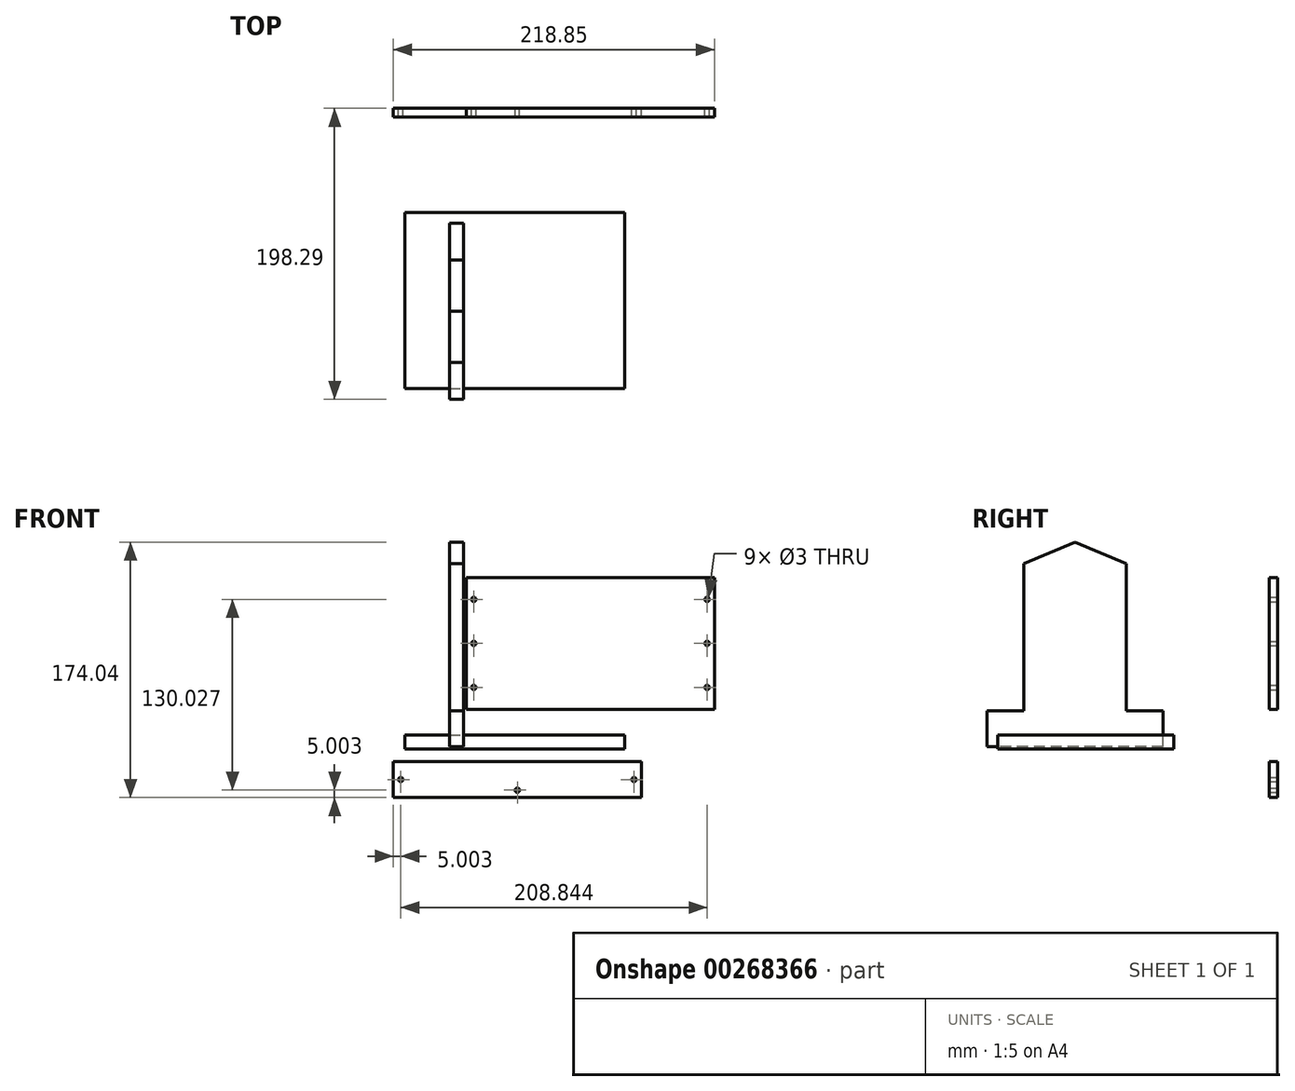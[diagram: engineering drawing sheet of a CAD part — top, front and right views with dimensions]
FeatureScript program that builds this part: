
annotation { "Feature Type Name" : "Feature", "Feature Type Description" : "" }
export const myFeature = defineFeature(function(context is Context, id is Id, definition is map)
    precondition{}
    {
        {
            var Q0;
            Q0=qCreatedBy(makeId("Top.planeOp"),FACE);
            var sketch = newSketch(context, id + "F0", { "sketchPlane" : qUnion([Q0])});
            skLineSegment(sketch, "E0.bottom", {"start": v(-30.55, -70.86) * mm, "end": v(119.45, -70.86) * mm});
            skLineSegment(sketch, "E0.top", {"start": v(-30.55, -190.86) * mm, "end": v(119.45, -190.86) * mm});
            skLineSegment(sketch, "E0.left", {"start": v(-30.55, -70.86) * mm, "end": v(-30.55, -190.86) * mm});
            skLineSegment(sketch, "E0.right", {"start": v(119.45, -70.86) * mm, "end": v(119.45, -190.86) * mm});
            skSolve(sketch);
        }
        {
            var Q0;
            Q0 = qSketchRegion(id + "F0", true);
            extrude(context, id + "F1", {"entities" : qUnion([Q0]), "depth" : 9.5 * mm});
        }
        {
            var Q0;
            Q0=qCreatedBy(makeId("Right.planeOp"),FACE);
            var sketch = newSketch(context, id + "F2", { "sketchPlane" : qUnion([Q0])});
            skLineSegment(sketch, "E1.bottom", {"start": v(-103.3, 1.37) * mm, "end": v(-173.3, 1.37) * mm});
            skLineSegment(sketch, "E1.left", {"start": v(-103.3, 25.87) * mm, "end": v(-103.3, 126.38) * mm});
            skLineSegment(sketch, "E1.right", {"start": v(-173.3, 25.87) * mm, "end": v(-173.3, 126.38) * mm});
            skLineSegment(sketch, "E2", {"start": v(-138.3, 140.87) * mm, "end": v(-103.3, 126.38) * mm});
            skLineSegment(sketch, "E3", {"start": v(-138.3, 140.87) * mm, "end": v(-173.3, 126.38) * mm});
            skPoint(sketch, "E4.orphan", {"position": v(-173.3, 140.87) * mm});
            skPoint(sketch, "E5.orphan", {"position": v(-103.3, 140.87) * mm});
            skLineSegment(sketch, "E6", {"start": v(-173.3, 1.37) * mm, "end": v(-198.3, 1.37) * mm});
            skLineSegment(sketch, "E7", {"start": v(-198.3, 1.37) * mm, "end": v(-198.3, 25.87) * mm});
            skLineSegment(sketch, "E8", {"start": v(-198.3, 25.87) * mm, "end": v(-173.3, 25.87) * mm});
            skLineSegment(sketch, "E9", {"start": v(-103.3, 1.37) * mm, "end": v(-78.3, 1.37) * mm});
            skLineSegment(sketch, "E10", {"start": v(-78.3, 1.37) * mm, "end": v(-78.3, 25.87) * mm});
            skLineSegment(sketch, "E11", {"start": v(-78.3, 25.87) * mm, "end": v(-103.3, 25.87) * mm});
            skSolve(sketch);
        }
        {
            var Q0;
            Q0 = qSketchRegion(id + "F2", true);
            extrude(context, id + "F3", {"entities" : qUnion([Q0]), "depth" : 9.5 * mm});
        }
        {
            var Q0;
            Q0=qCreatedBy(makeId("Front.planeOp"),FACE);
            var sketch = newSketch(context, id + "F4", { "sketchPlane" : qUnion([Q0])});
            skLineSegment(sketch, "E12.bottom", {"start": v(11.63, 26.86) * mm, "end": v(180.63, 26.86) * mm});
            skLineSegment(sketch, "E12.top", {"start": v(11.63, 116.86) * mm, "end": v(180.63, 116.86) * mm});
            skLineSegment(sketch, "E12.left", {"start": v(11.63, 26.86) * mm, "end": v(11.63, 116.86) * mm});
            skLineSegment(sketch, "E12.right", {"start": v(180.63, 26.86) * mm, "end": v(180.63, 116.86) * mm});
            skCircle(sketch, "E13", {"center": v(175.63, 101.86) * mm, "radius": 1.5 * mm});
            skCircle(sketch, "E14.0.1.0", {"center": v(175.63, 71.86) * mm, "radius": 1.5 * mm});
            skCircle(sketch, "E14.0.2.0", {"center": v(175.63, 41.86) * mm, "radius": 1.5 * mm});
            skLineSegment(sketch, "E14.direction1", {"start": v(175.63, 101.86) * mm, "end": v(200.63, 101.86) * mm, "construction": true});
            skLineSegment(sketch, "E14.direction2", {"start": v(175.63, 101.86) * mm, "end": v(175.63, 71.86) * mm, "construction": true});
            skLineSegment(sketch, "E15", {"start": v(96.13, 116.86) * mm, "end": v(96.13, 67.31) * mm, "construction": true});
            skCircle(sketch, "E16.MirrorC", {"center": v(16.63, 101.86) * mm, "radius": 1.5 * mm});
            skCircle(sketch, "E17.MirrorC", {"center": v(16.63, 41.86) * mm, "radius": 1.5 * mm});
            skCircle(sketch, "E18.MirrorC", {"center": v(16.63, 71.86) * mm, "radius": 1.5 * mm});
            skSolve(sketch);
        }
        {
            var Q0;
            Q0 = qSketchRegion(id + "F4", true);
            extrude(context, id + "F5", {"entities" : qUnion([Q0]), "depth" : 6 * mm});
        }
        {
            var Q0;
            Q0=qCreatedBy(makeId("Front.planeOp"),FACE);
            var sketch = newSketch(context, id + "F6", { "sketchPlane" : qUnion([Q0])});
            skLineSegment(sketch, "E19.bottom", {"start": v(-38.22, -33.17) * mm, "end": v(130.78, -33.17) * mm});
            skLineSegment(sketch, "E19.top", {"start": v(-38.22, -8.67) * mm, "end": v(130.78, -8.67) * mm});
            skLineSegment(sketch, "E19.left", {"start": v(-38.22, -33.17) * mm, "end": v(-38.22, -8.67) * mm});
            skLineSegment(sketch, "E19.right", {"start": v(130.78, -33.17) * mm, "end": v(130.78, -8.67) * mm});
            skCircle(sketch, "E20", {"center": v(-33.22, -20.92) * mm, "radius": 1.5 * mm});
            skLineSegment(sketch, "E21", {"start": v(46.28, -8.67) * mm, "end": v(46.28, -30.77) * mm, "construction": true});
            skCircle(sketch, "E22.MirrorC", {"center": v(125.78, -20.92) * mm, "radius": 1.5 * mm});
            skCircle(sketch, "E23", {"center": v(46.28, -28.17) * mm, "radius": 1.5 * mm});
            skSolve(sketch);
        }
        {
            var Q0;
            Q0=makeQuery(id+"F6.imprint","IMPRINT",FACE,{"disambiguationData":[TD([[makeQuery(id+"F6.imprint","IMPRINT",EDGE,{"derivedFrom":sQuery(id+"F6.wireOp",EDGE,"E19.bottom")}),1.0]])]});
            extrude(context, id + "F7", {"entities" : qUnion([Q0]), "depth" : 6 * mm});
        }
    });
